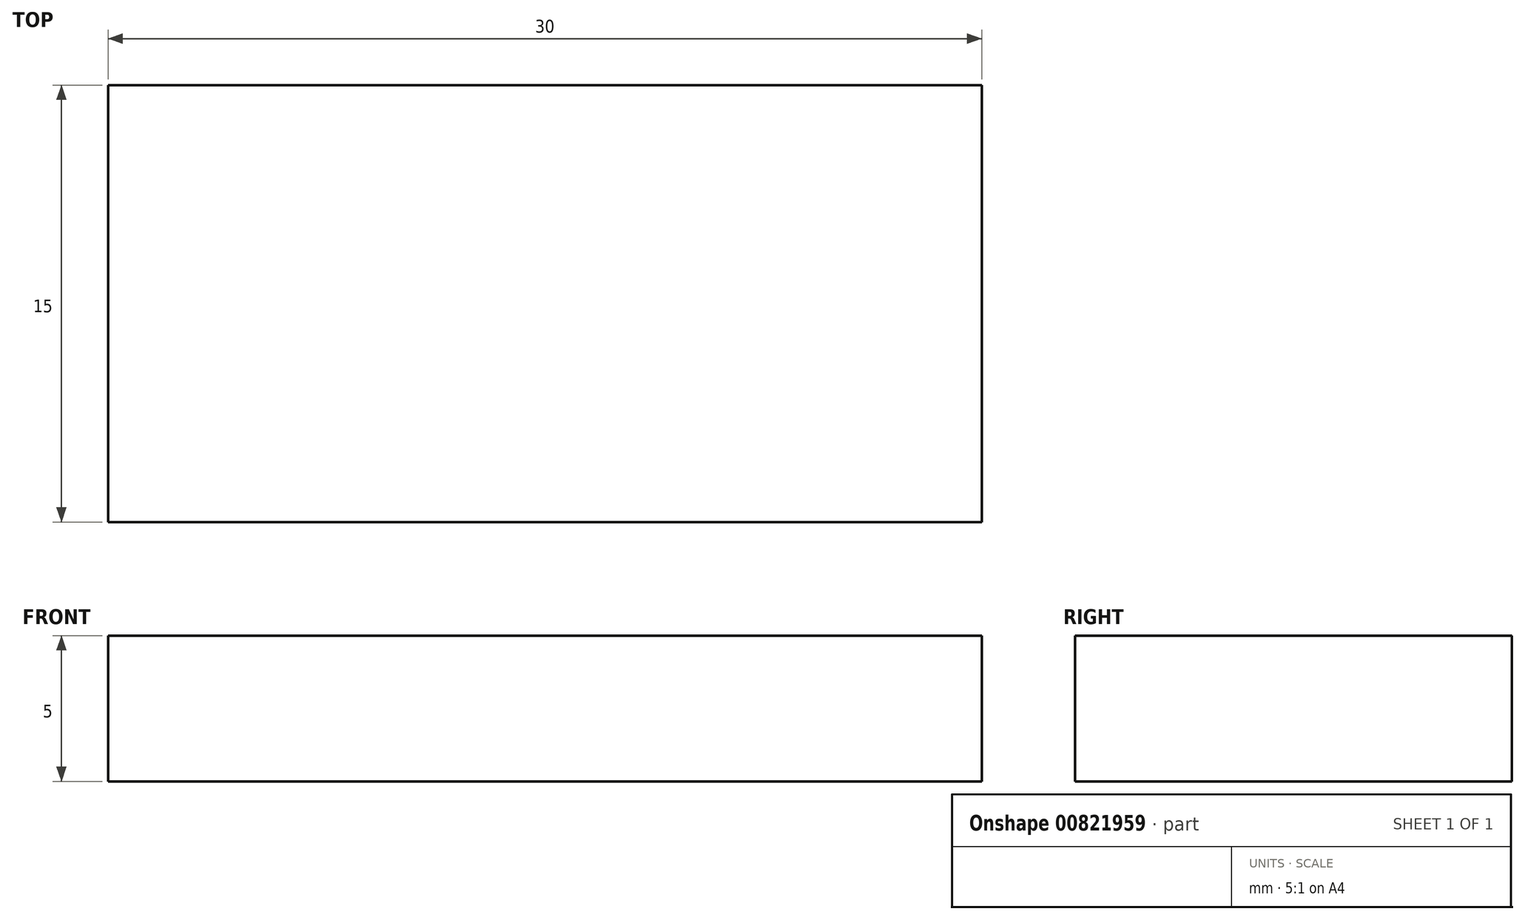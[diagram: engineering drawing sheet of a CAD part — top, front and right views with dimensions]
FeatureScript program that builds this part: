
annotation { "Feature Type Name" : "Feature", "Feature Type Description" : "" }
export const myFeature = defineFeature(function(context is Context, id is Id, definition is map)
    precondition{}
    {
        {
            var Q0;
            Q0=qCreatedBy(makeId("Top.planeOp"),FACE);
            var sketch = newSketch(context, id + "F0", { "sketchPlane" : qUnion([Q0])});
            skLineSegment(sketch, "E0.bottom", {"start": v(0, 0) * mm, "end": v(30, 0) * mm});
            skLineSegment(sketch, "E0.top", {"start": v(0, 15) * mm, "end": v(30, 15) * mm});
            skLineSegment(sketch, "E0.left", {"start": v(0, 0) * mm, "end": v(0, 15) * mm});
            skLineSegment(sketch, "E0.right", {"start": v(30, 0) * mm, "end": v(30, 15) * mm});
            skSolve(sketch);
        }
        {
            var Q0;
            Q0=makeQuery(id+"F0.imprint","IMPRINT",FACE,{"disambiguationData":[TD([[makeQuery(id+"F0.imprint","IMPRINT",EDGE,{"derivedFrom":sQuery(id+"F0.wireOp",EDGE,"E0.bottom")}),1.0]])]});
            extrude(context, id + "F1", {"entities" : qUnion([Q0]), "depth" : 5 * mm, "offsetDistance" : 25 * mm});
        }
    });
